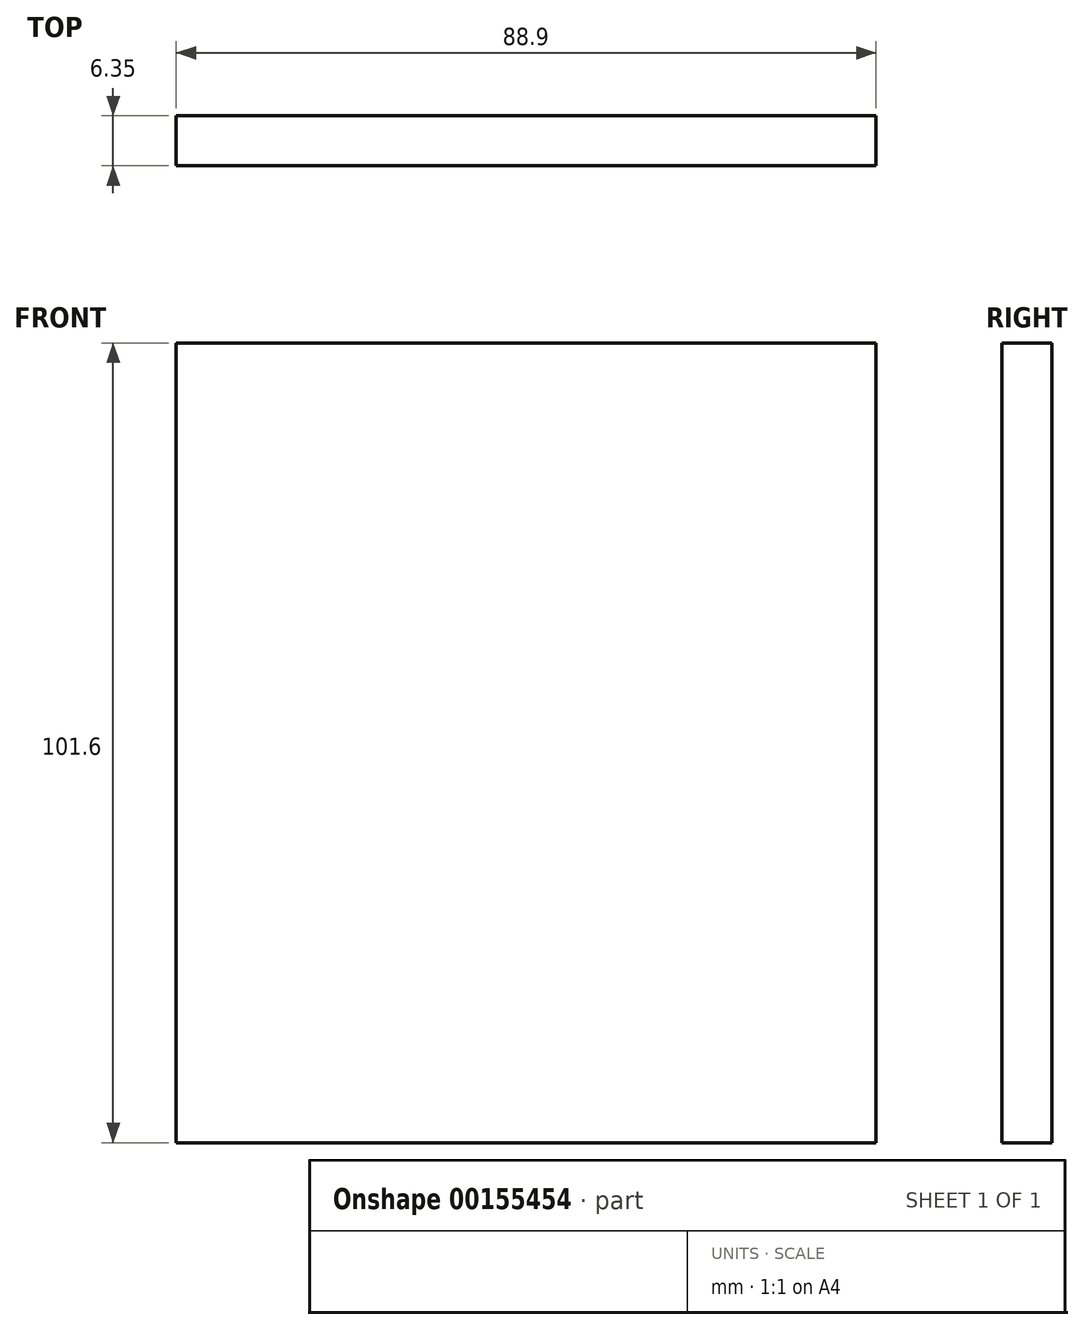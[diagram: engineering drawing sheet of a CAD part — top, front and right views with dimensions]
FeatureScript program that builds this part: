
annotation { "Feature Type Name" : "Feature", "Feature Type Description" : "" }
export const myFeature = defineFeature(function(context is Context, id is Id, definition is map)
    precondition{}
    {
        {
            var Q0;
            Q0=qCreatedBy(makeId("Front.planeOp"),FACE);
            var sketch = newSketch(context, id + "F0", { "sketchPlane" : qUnion([Q0])});
            skLineSegment(sketch, "E0.bottom", {"start": v(0, 0) * mm, "end": v(88.9, 0) * mm});
            skLineSegment(sketch, "E0.top", {"start": v(0, -101.6) * mm, "end": v(88.9, -101.6) * mm});
            skLineSegment(sketch, "E0.left", {"start": v(0, 0) * mm, "end": v(0, -101.6) * mm});
            skLineSegment(sketch, "E0.right", {"start": v(88.9, 0) * mm, "end": v(88.9, -101.6) * mm});
            skSolve(sketch);
        }
        {
            var Q0;
            Q0 = qSketchRegion(id + "F0", true);
            extrude(context, id + "F1", {"entities" : qUnion([Q0]), "depth" : 6.35 * mm});
        }
    });
